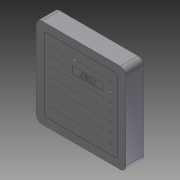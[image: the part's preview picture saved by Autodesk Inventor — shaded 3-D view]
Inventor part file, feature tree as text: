
AUTODESK INVENTOR PART (.ipt)
format: ipt  version: 2012 (Build 160160000, 160)  size: 348,160 bytes
history: native  units: in
note: dims shown in document units (in); Inventor stores cm internally (conversion verified against a paired STEP export)
features: extrude x12, sketch x12, plane x1
ambient origin geometry x8: Origin, YZ Plane, XZ Plane, XY Plane, X Axis, Y Axis, Z Axis, Center Point
bodies: Solid1 (feature_tree)
feature tree (25):
  extrude  "Extrusion1"  Depth=5.0in
  extrude  "Extrusion2"  Depth=1.0in TaperAngle=0.0deg
  extrude  "Extrusion3"  Depth=0.0625in
  extrude  "Extrusion4"  Depth=0.0625in
  extrude  "Extrusion6"  Depth=0.9375in
  extrude  "Extrusion7"  Depth=4.12in
  extrude  "Extrusion5"  Depth=0.0156in
  extrude  "Extrusion8"  Depth=0.0156in
  extrude  "Extrusion9"  Depth=0.0156in
  extrude  "Extrusion10"  Depth=0.44in
  plane  "Work Plane2"
  extrude  "Extrusion11"  Depth=0.0312in TaperAngle=0.0deg
  extrude  "Extrusion12"  Depth=0.05in
  sketch  "Sketch1"  dims[d0=5.0in d1=5.0in]
  sketch  "Sketch2"  dims[d2=0.3125in d3=1.0in d4=0.0in]
  sketch  "Sketch3"  dims[d6=0.0625in d7=0.0625in]
  sketch  "Sketch4"  dims[d8=0.0625in d9=0.0625in]
  sketch  "Sketch5"  dims[d10=0.0625in d11=0.9375in]
  sketch  "Sketch6"  dims[d12=0.0in d15=4.12in]
  sketch  "Sketch7"  dims[d16=4.12in d17=0.0156in]
  sketch  "Sketch8"  dims[d18=0.0156in d19=0.0156in]
  sketch  "Sketch9"  dims[d20=0.0156in d21=0.0156in]
  sketch  "Sketch10"  dims[d22=0.44in d23=0.44in]
  sketch  "Sketch12"  dims[d24=0.08in d25=0.0312in d26=0.0in]
  sketch  "Sketch13"  dims[d27=0.975in d28=0.05in d29=0.76in d30=3.0in d31=1.9685in d33=0.5in d34=0.3937in d36=1.0in d38=0.7874in d40=3.0in d41=0.3937in d43=1.0in d45=1.0in d46=0.5in d47=0.0312in d48=0.0in d49=0.2in d50=1.25in d51=0.0312in d52=0.0in d53=0.15in d54=2.7559in d56=0.5in d57=0.3937in d59=1.0in d61=0.85in d62=1.0in d63=0.0312in d64=0.0in d65=0.0312in d66=0.0in d67=0.05in d68=0.39in d69=1.75in d70=1.3in d72=0.0156in d73=0.0in d74=0.045in d75=0.4in d76=0.95in d77=0.0312in d78=0.0in d79=4.3014in d80=0.3493in d81=1.2667in d82=0.6334in d83=0.0in d85=0.2854in d86=0.2854in d87=0.0625in d88=0.0625in d89=-0.0625in d90=4.1764in d91=0.0in d92=0.2756in d93=0.1181in d94=0.7874in d96=1.5in d97=0.7874in d99=3.25in d102=0.4087in d103=0.0in d104=0.5in d105=0.5in]
